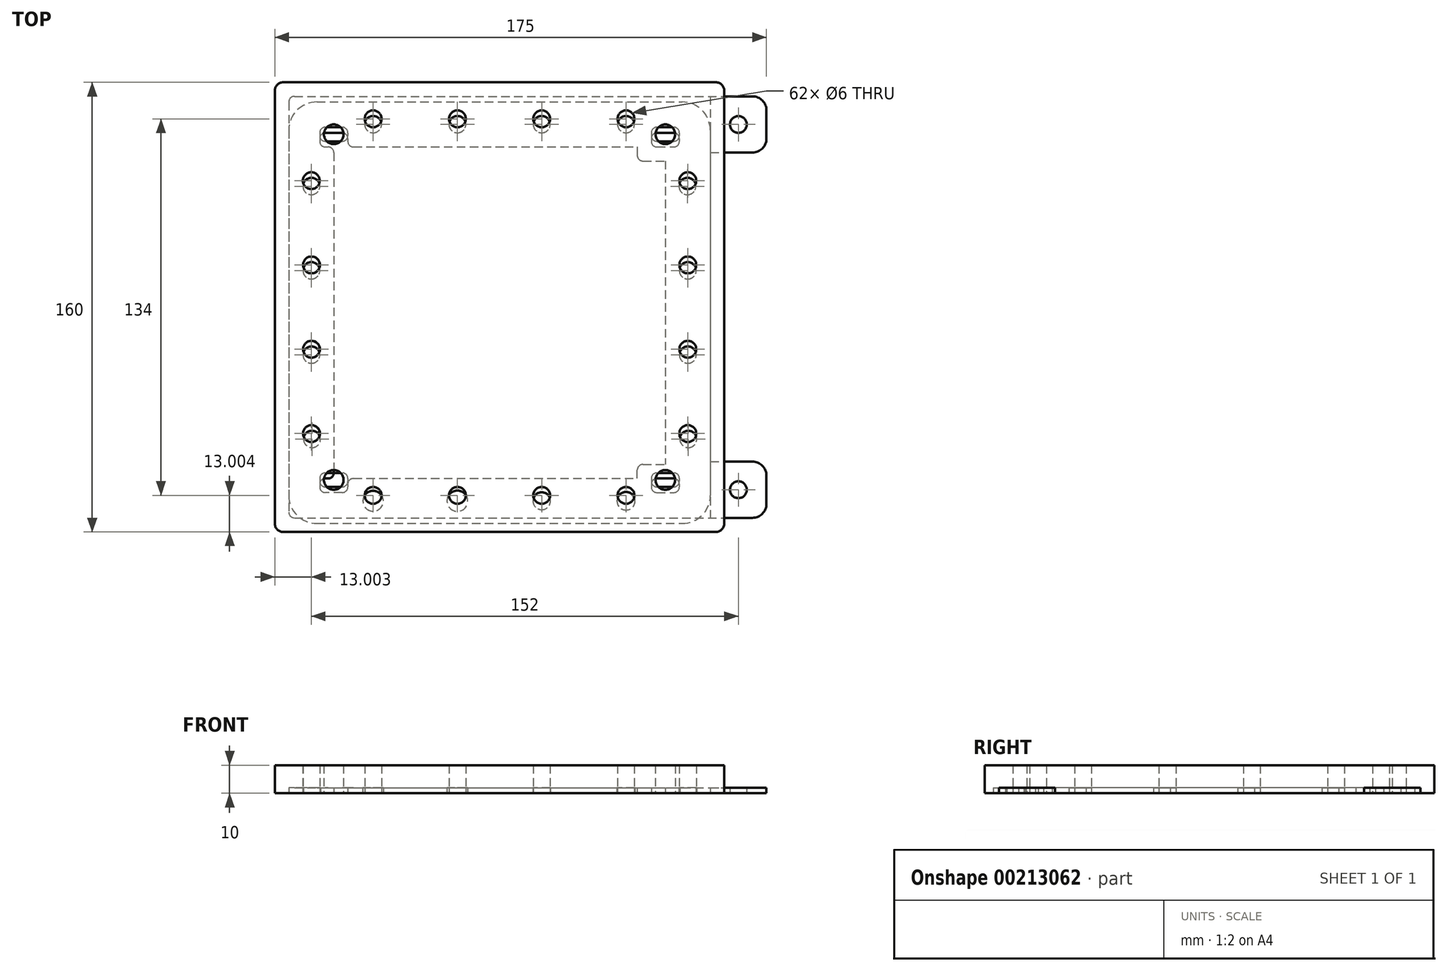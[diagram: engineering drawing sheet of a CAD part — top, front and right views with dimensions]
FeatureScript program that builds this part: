
annotation { "Feature Type Name" : "Feature", "Feature Type Description" : "" }
export const myFeature = defineFeature(function(context is Context, id is Id, definition is map)
    precondition{}
    {
        {
            var Q0;
            Q0=qCreatedBy(makeId("Top.planeOp"),FACE);
            var sketch = newSketch(context, id + "F0", { "sketchPlane" : qUnion([Q0])});
            skLineSegment(sketch, "E0.bottom", {"start": v(-66.98, 81.04) * mm, "end": v(81.02, 81.04) * mm});
            skLineSegment(sketch, "E0.top", {"start": v(-66.98, -68.96) * mm, "end": v(81.02, -68.96) * mm});
            skLineSegment(sketch, "E0.left", {"start": v(-68.98, 79.04) * mm, "end": v(-68.98, -66.96) * mm});
            skLineSegment(sketch, "E0.right", {"start": v(81.02, 81.04) * mm, "end": v(81.02, -68.96) * mm});
            skCircle(sketch, "E1", {"center": v(-60.98, 51.04) * mm, "radius": 3 * mm});
            skCircle(sketch, "E2", {"center": v(-60.98, 21.04) * mm, "radius": 3 * mm});
            skCircle(sketch, "E3", {"center": v(-60.98, -8.96) * mm, "radius": 3 * mm});
            skCircle(sketch, "E4", {"center": v(-60.98, -38.96) * mm, "radius": 3 * mm});
            skCircle(sketch, "E5", {"center": v(73.02, 51.04) * mm, "radius": 3 * mm});
            skCircle(sketch, "E6", {"center": v(73.02, 21.04) * mm, "radius": 3 * mm});
            skCircle(sketch, "E7", {"center": v(73.02, -8.96) * mm, "radius": 3 * mm});
            skCircle(sketch, "E8", {"center": v(73.02, -38.96) * mm, "radius": 3 * mm});
            skCircle(sketch, "E9", {"center": v(-38.98, 73.04) * mm, "radius": 3 * mm});
            skCircle(sketch, "E10", {"center": v(-8.98, 73.04) * mm, "radius": 3 * mm});
            skCircle(sketch, "E11", {"center": v(21.02, 73.04) * mm, "radius": 3 * mm});
            skCircle(sketch, "E12", {"center": v(51.02, 73.04) * mm, "radius": 3 * mm});
            skCircle(sketch, "E13", {"center": v(-38.98, -60.96) * mm, "radius": 3 * mm});
            skCircle(sketch, "E14", {"center": v(-8.98, -60.96) * mm, "radius": 3 * mm});
            skCircle(sketch, "E15", {"center": v(21.02, -60.96) * mm, "radius": 3 * mm});
            skCircle(sketch, "E16", {"center": v(51.02, -60.96) * mm, "radius": 3 * mm});
            skLineSegment(sketch, "E17.bottom", {"start": v(-55.98, 70.04) * mm, "end": v(-49.98, 70.04) * mm});
            skLineSegment(sketch, "E17.top", {"start": v(-55.98, 65.04) * mm, "end": v(-49.98, 65.04) * mm});
            skLineSegment(sketch, "E17.left", {"start": v(-57.98, 68.04) * mm, "end": v(-57.98, 67.04) * mm});
            skLineSegment(sketch, "E17.right", {"start": v(-47.98, 68.04) * mm, "end": v(-47.98, 67.04) * mm});
            skLineSegment(sketch, "E18.bottom", {"start": v(62.02, 70.04) * mm, "end": v(68.02, 70.04) * mm});
            skLineSegment(sketch, "E18.top", {"start": v(62.02, 65.04) * mm, "end": v(68.02, 65.04) * mm});
            skLineSegment(sketch, "E18.left", {"start": v(60.02, 68.04) * mm, "end": v(60.02, 67.04) * mm});
            skLineSegment(sketch, "E18.right", {"start": v(70.02, 68.04) * mm, "end": v(70.02, 67.04) * mm});
            skLineSegment(sketch, "E19.bottom", {"start": v(-55.98, -52.96) * mm, "end": v(-49.98, -52.96) * mm});
            skLineSegment(sketch, "E19.top", {"start": v(-55.98, -57.96) * mm, "end": v(-49.98, -57.96) * mm});
            skLineSegment(sketch, "E19.left", {"start": v(-57.98, -54.96) * mm, "end": v(-57.98, -55.96) * mm});
            skLineSegment(sketch, "E19.right", {"start": v(-47.98, -54.96) * mm, "end": v(-47.98, -55.96) * mm});
            skLineSegment(sketch, "E20.bottom", {"start": v(62.02, -52.96) * mm, "end": v(68.02, -52.96) * mm});
            skLineSegment(sketch, "E20.top", {"start": v(62.02, -57.96) * mm, "end": v(68.02, -57.96) * mm});
            skLineSegment(sketch, "E20.left", {"start": v(60.02, -54.96) * mm, "end": v(60.02, -55.96) * mm});
            skLineSegment(sketch, "E20.right", {"start": v(70.02, -54.96) * mm, "end": v(70.02, -55.96) * mm});
            skPoint(sketch, "E21.visualSharp", {"position": v(60.02, 70.04) * mm});
            skArc(sketch, "E21.filletArc", {"start": v(62.02, 70.04) * mm, "mid": v(60.6, 69.46) * mm, "end": v(60.02, 68.04) * mm});
            skPoint(sketch, "E22.visualSharp", {"position": v(70.02, 70.04) * mm});
            skArc(sketch, "E22.filletArc", {"start": v(70.02, 68.04) * mm, "mid": v(69.44, 69.46) * mm, "end": v(68.02, 70.04) * mm});
            skPoint(sketch, "E23.visualSharp", {"position": v(70.02, 65.04) * mm});
            skArc(sketch, "E23.filletArc", {"start": v(68.02, 65.04) * mm, "mid": v(69.44, 65.63) * mm, "end": v(70.02, 67.04) * mm});
            skPoint(sketch, "E24.visualSharp", {"position": v(60.02, 65.04) * mm});
            skArc(sketch, "E24.filletArc", {"start": v(60.02, 67.04) * mm, "mid": v(60.6, 65.63) * mm, "end": v(62.02, 65.04) * mm});
            skPoint(sketch, "E25.visualSharp", {"position": v(-47.98, 70.04) * mm});
            skArc(sketch, "E25.filletArc", {"start": v(-47.98, 68.04) * mm, "mid": v(-48.56, 69.46) * mm, "end": v(-49.98, 70.04) * mm});
            skPoint(sketch, "E26.visualSharp", {"position": v(-47.98, 65.04) * mm});
            skArc(sketch, "E26.filletArc", {"start": v(-49.98, 65.04) * mm, "mid": v(-48.56, 65.63) * mm, "end": v(-47.98, 67.04) * mm});
            skPoint(sketch, "E27.visualSharp", {"position": v(-57.98, 65.04) * mm});
            skArc(sketch, "E27.filletArc", {"start": v(-57.98, 67.04) * mm, "mid": v(-57.4, 65.63) * mm, "end": v(-55.98, 65.04) * mm});
            skPoint(sketch, "E28.visualSharp", {"position": v(-57.98, 70.04) * mm});
            skArc(sketch, "E28.filletArc", {"start": v(-55.98, 70.04) * mm, "mid": v(-57.4, 69.46) * mm, "end": v(-57.98, 68.04) * mm});
            skPoint(sketch, "E29.visualSharp", {"position": v(-57.98, -52.96) * mm});
            skArc(sketch, "E29.filletArc", {"start": v(-55.98, -52.96) * mm, "mid": v(-57.4, -53.54) * mm, "end": v(-57.98, -54.96) * mm});
            skPoint(sketch, "E30.visualSharp", {"position": v(-57.98, -57.96) * mm});
            skArc(sketch, "E30.filletArc", {"start": v(-57.98, -55.96) * mm, "mid": v(-57.4, -57.37) * mm, "end": v(-55.98, -57.96) * mm});
            skPoint(sketch, "E31.visualSharp", {"position": v(-47.98, -57.96) * mm});
            skArc(sketch, "E31.filletArc", {"start": v(-49.98, -57.96) * mm, "mid": v(-48.56, -57.37) * mm, "end": v(-47.98, -55.96) * mm});
            skPoint(sketch, "E32.visualSharp", {"position": v(-47.98, -52.96) * mm});
            skArc(sketch, "E32.filletArc", {"start": v(-47.98, -54.96) * mm, "mid": v(-48.56, -53.54) * mm, "end": v(-49.98, -52.96) * mm});
            skPoint(sketch, "E33.visualSharp", {"position": v(70.02, -52.96) * mm});
            skArc(sketch, "E33.filletArc", {"start": v(70.02, -54.96) * mm, "mid": v(69.44, -53.54) * mm, "end": v(68.02, -52.96) * mm});
            skPoint(sketch, "E34.visualSharp", {"position": v(70.02, -57.96) * mm});
            skArc(sketch, "E34.filletArc", {"start": v(68.02, -57.96) * mm, "mid": v(69.44, -57.37) * mm, "end": v(70.02, -55.96) * mm});
            skPoint(sketch, "E35.visualSharp", {"position": v(60.02, -57.96) * mm});
            skArc(sketch, "E35.filletArc", {"start": v(60.02, -55.96) * mm, "mid": v(60.6, -57.37) * mm, "end": v(62.02, -57.96) * mm});
            skPoint(sketch, "E36.visualSharp", {"position": v(60.02, -52.96) * mm});
            skArc(sketch, "E36.filletArc", {"start": v(62.02, -52.96) * mm, "mid": v(60.6, -53.54) * mm, "end": v(60.02, -54.96) * mm});
            skLineSegment(sketch, "E37.bottom", {"start": v(81.02, 81.04) * mm, "end": v(96.02, 81.04) * mm});
            skLineSegment(sketch, "E37.top", {"start": v(81.02, 61.04) * mm, "end": v(96.02, 61.04) * mm});
            skLineSegment(sketch, "E37.left", {"start": v(81.02, 81.04) * mm, "end": v(81.02, 61.04) * mm});
            skLineSegment(sketch, "E37.right", {"start": v(101.02, 76.04) * mm, "end": v(101.02, 66.04) * mm});
            skCircle(sketch, "E38", {"center": v(91.02, 71.04) * mm, "radius": 3 * mm});
            skPoint(sketch, "E38.centerSnap0", {"position": v(91.02, 61.04) * mm});
            skPoint(sketch, "E38.centerSnap1", {"position": v(101.02, 71.04) * mm});
            skPoint(sketch, "E39.visualSharp", {"position": v(101.02, 81.04) * mm});
            skArc(sketch, "E39.filletArc", {"start": v(101.02, 76.04) * mm, "mid": v(99.56, 79.58) * mm, "end": v(96.02, 81.04) * mm});
            skPoint(sketch, "E40.visualSharp", {"position": v(101.02, 61.04) * mm});
            skArc(sketch, "E40.filletArc", {"start": v(96.02, 61.04) * mm, "mid": v(99.56, 62.5) * mm, "end": v(101.02, 66.04) * mm});
            skLineSegment(sketch, "E41.bottom", {"start": v(81.02, -68.96) * mm, "end": v(96.02, -68.96) * mm});
            skLineSegment(sketch, "E41.top", {"start": v(81.02, -48.96) * mm, "end": v(96.02, -48.96) * mm});
            skLineSegment(sketch, "E41.left", {"start": v(81.02, -68.96) * mm, "end": v(81.02, -48.96) * mm});
            skLineSegment(sketch, "E41.right", {"start": v(101.02, -63.96) * mm, "end": v(101.02, -53.96) * mm});
            skCircle(sketch, "E42", {"center": v(91.02, -58.96) * mm, "radius": 3 * mm});
            skPoint(sketch, "E42.centerSnap0", {"position": v(101.02, -58.96) * mm});
            skPoint(sketch, "E42.centerSnap1", {"position": v(91.02, -48.96) * mm});
            skPoint(sketch, "E43.visualSharp", {"position": v(101.02, -48.96) * mm});
            skArc(sketch, "E43.filletArc", {"start": v(101.02, -53.96) * mm, "mid": v(99.56, -50.42) * mm, "end": v(96.02, -48.96) * mm});
            skPoint(sketch, "E44.visualSharp", {"position": v(101.02, -68.96) * mm});
            skArc(sketch, "E44.filletArc", {"start": v(96.02, -68.96) * mm, "mid": v(99.56, -67.5) * mm, "end": v(101.02, -63.96) * mm});
            skPoint(sketch, "E45.visualSharp", {"position": v(-68.98, 81.04) * mm});
            skArc(sketch, "E45.filletArc", {"start": v(-66.98, 81.04) * mm, "mid": v(-68.4, 80.46) * mm, "end": v(-68.98, 79.04) * mm});
            skPoint(sketch, "E46.visualSharp", {"position": v(-68.98, -68.96) * mm});
            skArc(sketch, "E46.filletArc", {"start": v(-68.98, -66.96) * mm, "mid": v(-68.4, -68.37) * mm, "end": v(-66.98, -68.96) * mm});
            skSolve(sketch);
        }
        {
            var Q0;
            Q0=qCreatedBy(makeId("Top.planeOp"),FACE);
            var sketch = newSketch(context, id + "F1", { "sketchPlane" : qUnion([Q0])});
            skLineSegment(sketch, "E47.bottom", {"start": v(-58.98, 79.04) * mm, "end": v(71.02, 79.04) * mm});
            skLineSegment(sketch, "E47.top", {"start": v(-58.98, -70.96) * mm, "end": v(71.02, -70.96) * mm});
            skLineSegment(sketch, "E47.left", {"start": v(-68.98, 69.04) * mm, "end": v(-68.98, -60.96) * mm});
            skLineSegment(sketch, "E47.right", {"start": v(81.02, 69.04) * mm, "end": v(81.02, -60.96) * mm});
            skLineSegment(sketch, "E48.top", {"start": v(-45.98, -54.96) * mm, "end": v(55.02, -54.96) * mm});
            skLineSegment(sketch, "E48.left", {"start": v(-52.98, 61.04) * mm, "end": v(-52.98, -52.96) * mm});
            skLineSegment(sketch, "E49.top", {"start": v(57.02, 58.04) * mm, "end": v(65.02, 58.04) * mm});
            skLineSegment(sketch, "E49.left", {"start": v(55.02, 63.04) * mm, "end": v(55.02, 60.04) * mm});
            skLineSegment(sketch, "E50", {"start": v(-45.98, 63.04) * mm, "end": v(55.02, 63.04) * mm});
            skLineSegment(sketch, "E51", {"start": v(65.02, 58.04) * mm, "end": v(65.02, -49.96) * mm});
            skLineSegment(sketch, "E52.bottom", {"start": v(62.02, 68.04) * mm, "end": v(68.02, 68.04) * mm});
            skLineSegment(sketch, "E52.top", {"start": v(62.02, 63.04) * mm, "end": v(68.02, 63.04) * mm});
            skLineSegment(sketch, "E52.left", {"start": v(60.02, 66.04) * mm, "end": v(60.02, 65.04) * mm});
            skLineSegment(sketch, "E52.right", {"start": v(70.02, 66.04) * mm, "end": v(70.02, 65.04) * mm});
            skPoint(sketch, "E53.visualSharp", {"position": v(70.02, 68.04) * mm});
            skArc(sketch, "E53.filletArc", {"start": v(70.02, 66.04) * mm, "mid": v(69.44, 67.46) * mm, "end": v(68.02, 68.04) * mm});
            skPoint(sketch, "E54.visualSharp", {"position": v(70.02, 63.04) * mm});
            skArc(sketch, "E54.filletArc", {"start": v(68.02, 63.04) * mm, "mid": v(69.44, 63.63) * mm, "end": v(70.02, 65.04) * mm});
            skPoint(sketch, "E55.visualSharp", {"position": v(60.02, 63.04) * mm});
            skArc(sketch, "E55.filletArc", {"start": v(60.02, 65.04) * mm, "mid": v(60.6, 63.63) * mm, "end": v(62.02, 63.04) * mm});
            skPoint(sketch, "E56.visualSharp", {"position": v(60.02, 68.04) * mm});
            skArc(sketch, "E56.filletArc", {"start": v(62.02, 68.04) * mm, "mid": v(60.6, 67.46) * mm, "end": v(60.02, 66.04) * mm});
            skPoint(sketch, "E57.visualSharp", {"position": v(55.02, 58.04) * mm});
            skArc(sketch, "E57.filletArc", {"start": v(55.02, 60.04) * mm, "mid": v(55.6, 58.63) * mm, "end": v(57.02, 58.04) * mm});
            skLineSegment(sketch, "E58.bottom", {"start": v(-55.98, 68.04) * mm, "end": v(-49.98, 68.04) * mm});
            skLineSegment(sketch, "E58.top", {"start": v(-55.98, 63.04) * mm, "end": v(-54.98, 63.04) * mm});
            skLineSegment(sketch, "E58.left", {"start": v(-57.98, 66.04) * mm, "end": v(-57.98, 65.04) * mm});
            skLineSegment(sketch, "E58.right", {"start": v(-47.98, 66.04) * mm, "end": v(-47.98, 65.04) * mm});
            skPoint(sketch, "E59.visualSharp", {"position": v(-57.98, 63.04) * mm});
            skArc(sketch, "E59.filletArc", {"start": v(-57.98, 65.04) * mm, "mid": v(-57.4, 63.63) * mm, "end": v(-55.98, 63.04) * mm});
            skPoint(sketch, "E60.visualSharp", {"position": v(-57.98, 68.04) * mm});
            skArc(sketch, "E60.filletArc", {"start": v(-55.98, 68.04) * mm, "mid": v(-57.4, 67.46) * mm, "end": v(-57.98, 66.04) * mm});
            skPoint(sketch, "E61.visualSharp", {"position": v(-47.98, 68.04) * mm});
            skArc(sketch, "E61.filletArc", {"start": v(-47.98, 66.04) * mm, "mid": v(-48.56, 67.46) * mm, "end": v(-49.98, 68.04) * mm});
            skPoint(sketch, "E62.visualSharp", {"position": v(-47.98, 63.04) * mm});
            skArc(sketch, "E62.filletArc", {"start": v(-47.98, 65.04) * mm, "mid": v(-47.4, 63.63) * mm, "end": v(-45.98, 63.04) * mm});
            skPoint(sketch, "E63.visualSharp", {"position": v(-52.98, 63.04) * mm});
            skArc(sketch, "E63.filletArc", {"start": v(-52.98, 61.04) * mm, "mid": v(-53.56, 62.46) * mm, "end": v(-54.98, 63.04) * mm});
            skCircle(sketch, "E64", {"center": v(-38.98, 71.06) * mm, "radius": 3 * mm});
            skCircle(sketch, "E65", {"center": v(-8.98, 71.06) * mm, "radius": 3 * mm});
            skCircle(sketch, "E66", {"center": v(21.02, 71.06) * mm, "radius": 3 * mm});
            skCircle(sketch, "E67", {"center": v(51.02, 71.06) * mm, "radius": 3 * mm});
            skCircle(sketch, "E68", {"center": v(72.89, 49.04) * mm, "radius": 3 * mm});
            skCircle(sketch, "E69", {"center": v(73.02, 19.04) * mm, "radius": 3 * mm});
            skCircle(sketch, "E70", {"center": v(73.02, -10.96) * mm, "radius": 3 * mm});
            skCircle(sketch, "E71", {"center": v(-60.94, 49.04) * mm, "radius": 3 * mm});
            skCircle(sketch, "E72", {"center": v(-60.94, 19.04) * mm, "radius": 3 * mm});
            skCircle(sketch, "E73", {"center": v(-60.94, -10.96) * mm, "radius": 3 * mm});
            skCircle(sketch, "E74", {"center": v(-60.72, -40.96) * mm, "radius": 3 * mm});
            skCircle(sketch, "E75", {"center": v(73.2, -40.96) * mm, "radius": 3 * mm});
            skLineSegment(sketch, "E76.bottom", {"start": v(62.02, -54.96) * mm, "end": v(68.02, -54.96) * mm});
            skLineSegment(sketch, "E76.top", {"start": v(62.02, -59.96) * mm, "end": v(68.02, -59.96) * mm});
            skLineSegment(sketch, "E76.left", {"start": v(60.02, -56.96) * mm, "end": v(60.02, -57.96) * mm});
            skLineSegment(sketch, "E76.right", {"start": v(70.02, -56.96) * mm, "end": v(70.02, -57.96) * mm});
            skLineSegment(sketch, "E77", {"start": v(55.02, -54.96) * mm, "end": v(55.02, -51.96) * mm});
            skLineSegment(sketch, "E78", {"start": v(57.02, -49.96) * mm, "end": v(65.02, -49.96) * mm});
            skPoint(sketch, "E79.visualSharp", {"position": v(55.02, -49.96) * mm});
            skArc(sketch, "E79.filletArc", {"start": v(57.02, -49.96) * mm, "mid": v(55.6, -50.54) * mm, "end": v(55.02, -51.96) * mm});
            skPoint(sketch, "E80.visualSharp", {"position": v(60.02, -54.96) * mm});
            skArc(sketch, "E80.filletArc", {"start": v(62.02, -54.96) * mm, "mid": v(60.6, -55.54) * mm, "end": v(60.02, -56.96) * mm});
            skPoint(sketch, "E81.visualSharp", {"position": v(60.02, -59.96) * mm});
            skArc(sketch, "E81.filletArc", {"start": v(60.02, -57.96) * mm, "mid": v(60.6, -59.37) * mm, "end": v(62.02, -59.96) * mm});
            skPoint(sketch, "E82.visualSharp", {"position": v(70.02, -59.96) * mm});
            skArc(sketch, "E82.filletArc", {"start": v(68.02, -59.96) * mm, "mid": v(69.44, -59.37) * mm, "end": v(70.02, -57.96) * mm});
            skPoint(sketch, "E83.visualSharp", {"position": v(70.02, -54.96) * mm});
            skArc(sketch, "E83.filletArc", {"start": v(70.02, -56.96) * mm, "mid": v(69.44, -55.54) * mm, "end": v(68.02, -54.96) * mm});
            skCircle(sketch, "E84", {"center": v(-38.98, -62.96) * mm, "radius": 3.64 * mm});
            skCircle(sketch, "E85", {"center": v(-8.98, -62.96) * mm, "radius": 3.7 * mm});
            skCircle(sketch, "E86", {"center": v(21.02, -62.96) * mm, "radius": 3.1 * mm});
            skCircle(sketch, "E87", {"center": v(51.02, -62.96) * mm, "radius": 3.22 * mm});
            skLineSegment(sketch, "E88.bottom", {"start": v(-54.98, -54.96) * mm, "end": v(-55.98, -54.96) * mm});
            skLineSegment(sketch, "E88.top", {"start": v(-49.98, -59.96) * mm, "end": v(-55.98, -59.96) * mm});
            skLineSegment(sketch, "E88.left", {"start": v(-47.98, -56.96) * mm, "end": v(-47.98, -57.96) * mm});
            skLineSegment(sketch, "E88.right", {"start": v(-57.98, -56.96) * mm, "end": v(-57.98, -57.96) * mm});
            skPoint(sketch, "E89.visualSharp", {"position": v(-57.98, -54.96) * mm});
            skArc(sketch, "E89.filletArc", {"start": v(-55.98, -54.96) * mm, "mid": v(-57.4, -55.54) * mm, "end": v(-57.98, -56.96) * mm});
            skPoint(sketch, "E90.visualSharp", {"position": v(-47.98, -59.96) * mm});
            skArc(sketch, "E90.filletArc", {"start": v(-49.98, -59.96) * mm, "mid": v(-48.56, -59.37) * mm, "end": v(-47.98, -57.96) * mm});
            skPoint(sketch, "E91.visualSharp", {"position": v(-47.98, -54.96) * mm});
            skArc(sketch, "E91.filletArc", {"start": v(-45.98, -54.96) * mm, "mid": v(-47.4, -55.54) * mm, "end": v(-47.98, -56.96) * mm});
            skPoint(sketch, "E92.visualSharp", {"position": v(-57.98, -59.96) * mm});
            skArc(sketch, "E92.filletArc", {"start": v(-57.98, -57.96) * mm, "mid": v(-57.4, -59.37) * mm, "end": v(-55.98, -59.96) * mm});
            skPoint(sketch, "E93.visualSharp", {"position": v(-52.98, -54.96) * mm});
            skArc(sketch, "E93.filletArc", {"start": v(-54.98, -54.96) * mm, "mid": v(-53.56, -54.37) * mm, "end": v(-52.98, -52.96) * mm});
            skPoint(sketch, "E94.visualSharp", {"position": v(81.02, 79.04) * mm});
            skArc(sketch, "E94.filletArc", {"start": v(81.02, 69.04) * mm, "mid": v(78.1, 76.12) * mm, "end": v(71.02, 79.04) * mm});
            skPoint(sketch, "E95.visualSharp", {"position": v(81.02, -70.96) * mm});
            skArc(sketch, "E95.filletArc", {"start": v(71.02, -70.96) * mm, "mid": v(78.1, -68.03) * mm, "end": v(81.02, -60.96) * mm});
            skPoint(sketch, "E96.visualSharp", {"position": v(-68.98, -70.96) * mm});
            skArc(sketch, "E96.filletArc", {"start": v(-68.98, -60.96) * mm, "mid": v(-66.05, -68.03) * mm, "end": v(-58.98, -70.96) * mm});
            skPoint(sketch, "E97.visualSharp", {"position": v(-68.98, 79.04) * mm});
            skArc(sketch, "E97.filletArc", {"start": v(-58.98, 79.04) * mm, "mid": v(-66.05, 76.12) * mm, "end": v(-68.98, 69.04) * mm});
            skSolve(sketch);
        }
        {
            var Q0;
            Q0=makeQuery(id+"F1.imprint","IMPRINT",FACE,{"disambiguationData":[TD([[makeQuery(id+"F1.imprint","IMPRINT",EDGE,{"derivedFrom":sQuery(id+"F1.wireOp",EDGE,"E47.bottom")}),-1.0]])]});
            extrude(context, id + "F2", {"entities" : qUnion([Q0]), "depth" : 2 * mm});
        }
        {
            var Q0;
            Q0 = qSketchRegion(id + "F0", true);
            extrude(context, id + "F3", {"entities" : qUnion([Q0]), "depth" : 2 * mm});
        }
        {
            var Q0;
            Q0=makeQuery(id+"F0.imprint","IMPRINT",FACE,{"disambiguationData":[TD([[makeQuery(id+"F0.imprint","IMPRINT",EDGE,{"derivedFrom":sQuery(id+"F0.wireOp",EDGE,"E0.bottom")}),-1.0]])]});
            extrude(context, id + "F4", {"entities" : qUnion([Q0]), "depth" : 2 * mm});
        }
        {
            var Q0;
            Q0=qCreatedBy(makeId("Top.planeOp"),FACE);
            var sketch = newSketch(context, id + "F5", { "sketchPlane" : qUnion([Q0])});
            skLineSegment(sketch, "E98.bottom", {"start": v(-70.98, 86.04) * mm, "end": v(83.02, 86.04) * mm});
            skLineSegment(sketch, "E98.top", {"start": v(-70.98, -73.96) * mm, "end": v(83.02, -73.96) * mm});
            skLineSegment(sketch, "E98.left", {"start": v(-73.98, 83.04) * mm, "end": v(-73.98, -70.96) * mm});
            skLineSegment(sketch, "E98.right", {"start": v(86.02, 83.04) * mm, "end": v(86.02, -70.96) * mm});
            skCircle(sketch, "E99", {"center": v(-52.98, 67.54) * mm, "radius": 3.5 * mm});
            skCircle(sketch, "E100", {"center": v(65.02, 67.54) * mm, "radius": 3.5 * mm});
            skCircle(sketch, "E101", {"center": v(-52.98, -55.46) * mm, "radius": 3.5 * mm});
            skCircle(sketch, "E102", {"center": v(65.02, -55.46) * mm, "radius": 3.5 * mm});
            skCircle(sketch, "E103", {"center": v(-38.98, -60.96) * mm, "radius": 3 * mm});
            skCircle(sketch, "E104", {"center": v(-8.98, -60.96) * mm, "radius": 3 * mm});
            skCircle(sketch, "E105", {"center": v(21.02, -60.96) * mm, "radius": 3 * mm});
            skCircle(sketch, "E106", {"center": v(51.02, -60.96) * mm, "radius": 3 * mm});
            skCircle(sketch, "E107", {"center": v(73.02, -38.96) * mm, "radius": 3 * mm});
            skCircle(sketch, "E108", {"center": v(73.02, -8.96) * mm, "radius": 3 * mm});
            skCircle(sketch, "E109", {"center": v(73.02, 21.04) * mm, "radius": 3 * mm});
            skCircle(sketch, "E110", {"center": v(73.02, 51.04) * mm, "radius": 3 * mm});
            skCircle(sketch, "E111", {"center": v(51.02, 73.04) * mm, "radius": 3 * mm});
            skCircle(sketch, "E112", {"center": v(21.02, 73.04) * mm, "radius": 3 * mm});
            skCircle(sketch, "E113", {"center": v(-8.98, 73.04) * mm, "radius": 3 * mm});
            skCircle(sketch, "E114", {"center": v(-38.98, 73.04) * mm, "radius": 3 * mm});
            skCircle(sketch, "E115", {"center": v(-60.98, 51.04) * mm, "radius": 3 * mm});
            skCircle(sketch, "E116", {"center": v(-60.91, 21.04) * mm, "radius": 3 * mm});
            skCircle(sketch, "E117", {"center": v(-60.91, -8.96) * mm, "radius": 3 * mm});
            skCircle(sketch, "E118", {"center": v(-60.91, -38.96) * mm, "radius": 3 * mm});
            skPoint(sketch, "E119.visualSharp", {"position": v(-73.98, 86.04) * mm});
            skArc(sketch, "E119.filletArc", {"start": v(-70.98, 86.04) * mm, "mid": v(-73.1, 85.17) * mm, "end": v(-73.98, 83.04) * mm});
            skPoint(sketch, "E120.visualSharp", {"position": v(86.02, 86.04) * mm});
            skArc(sketch, "E120.filletArc", {"start": v(86.02, 83.04) * mm, "mid": v(85.14, 85.17) * mm, "end": v(83.02, 86.04) * mm});
            skPoint(sketch, "E121.visualSharp", {"position": v(-73.98, -73.96) * mm});
            skArc(sketch, "E121.filletArc", {"start": v(-73.98, -70.96) * mm, "mid": v(-73.1, -73.08) * mm, "end": v(-70.98, -73.96) * mm});
            skPoint(sketch, "E122.visualSharp", {"position": v(86.02, -73.96) * mm});
            skArc(sketch, "E122.filletArc", {"start": v(83.02, -73.96) * mm, "mid": v(85.14, -73.08) * mm, "end": v(86.02, -70.96) * mm});
            skSolve(sketch);
        }
        {
            var Q0;
            Q0=makeQuery(id+"F5.imprint","IMPRINT",FACE,{"disambiguationData":[TD([[makeQuery(id+"F5.imprint","IMPRINT",EDGE,{"derivedFrom":sQuery(id+"F5.wireOp",EDGE,"E98.bottom")}),-1.0]])]});
            extrude(context, id + "F6", {"entities" : qUnion([Q0]), "depth" : 10 * mm});
        }
    });
